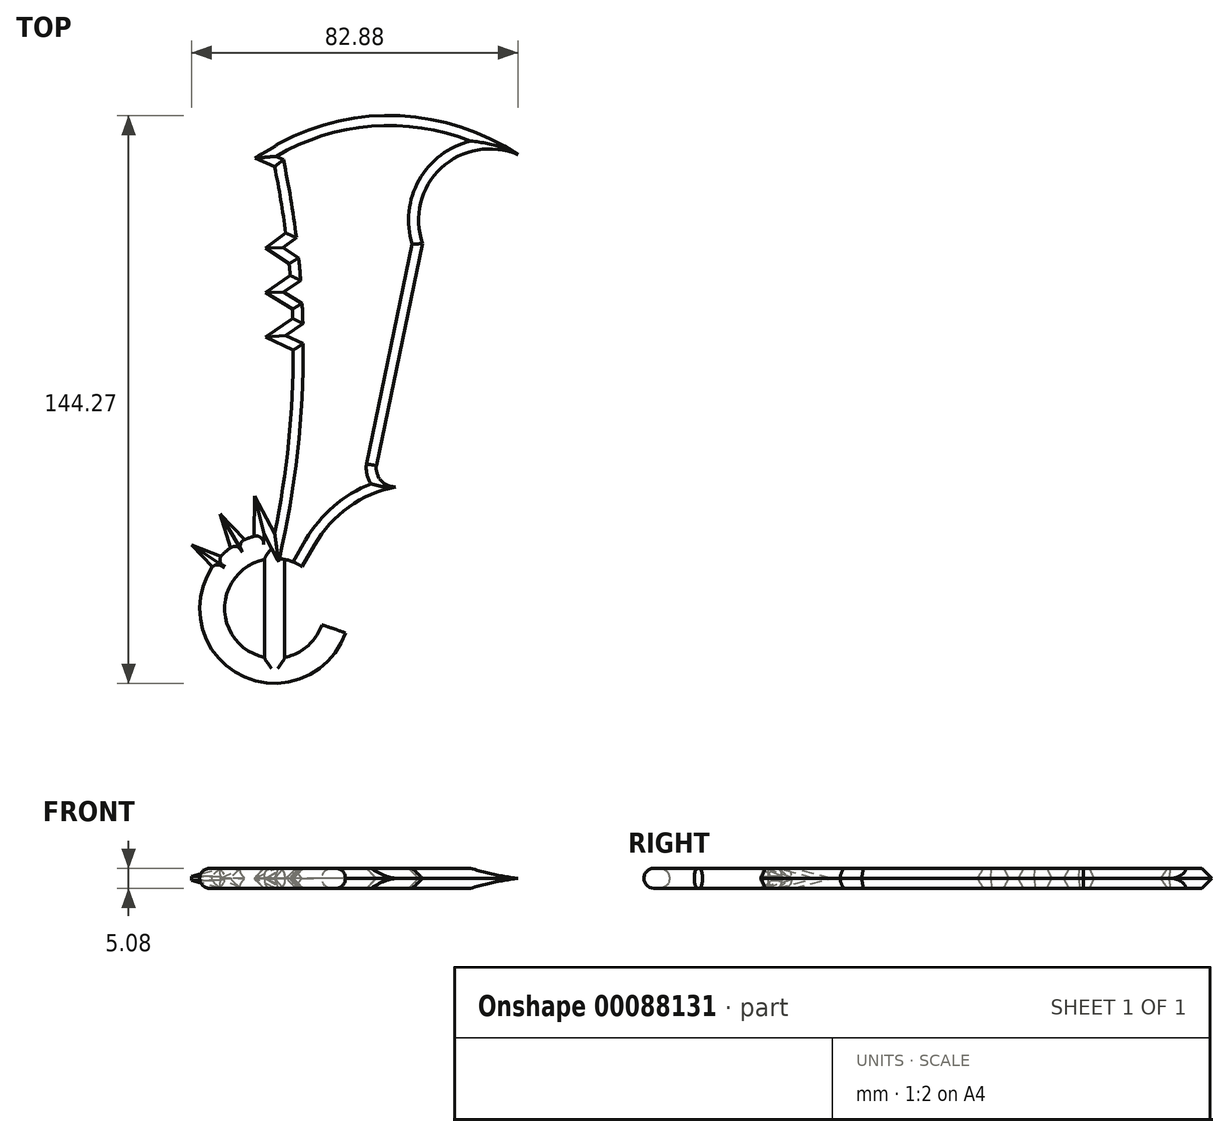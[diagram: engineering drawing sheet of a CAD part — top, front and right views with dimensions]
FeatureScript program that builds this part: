
annotation { "Feature Type Name" : "Feature", "Feature Type Description" : "" }
export const myFeature = defineFeature(function(context is Context, id is Id, definition is map)
    precondition{}
    {
        {
            var Q0;
            Q0=qCreatedBy(makeId("Top.planeOp"),FACE);
            var sketch = newSketch(context, id + "F0", { "sketchPlane" : qUnion([Q0])});
            skArc(sketch, "E0", {"start": v(10.12, 16.14) * mm, "mid": v(5.26, 18.3) * mm, "end": v(0, 19.05) * mm});
            skArc(sketch, "E1", {"start": v(6.94, 10.64) * mm, "mid": v(-12.02, -4.11) * mm, "end": v(12, -4.15) * mm});
            skLineSegment(sketch, "E2", {"start": v(0, 0) * mm, "end": v(-2.54, 0) * mm});
            skLineSegment(sketch, "E3", {"start": v(0, 0) * mm, "end": v(2.54, 0) * mm});
            skLineSegment(sketch, "E4", {"start": v(2.54, 0) * mm, "end": v(2.54, 12.44) * mm});
            skLineSegment(sketch, "E5", {"start": v(-2.54, 12.44) * mm, "end": v(-2.54, -12.44) * mm});
            skLineSegment(sketch, "E6", {"start": v(2.54, 0) * mm, "end": v(2.54, -12.44) * mm});
            skLineSegment(sketch, "E7", {"start": v(6.94, 10.64) * mm, "end": v(10.12, 16.14) * mm});
            skLineSegment(sketch, "E8", {"start": v(12, -4.15) * mm, "end": v(18, -6.23) * mm});
            skArc(sketch, "E9", {"start": v(0, 19.05) * mm, "mid": v(3.55, 42.22) * mm, "end": v(4.74, 65.62) * mm});
            skArc(sketch, "E10", {"start": v(61.8, 115.25) * mm, "mid": v(31.92, 125.15) * mm, "end": v(1.21, 118.24) * mm});
            skLineSegment(sketch, "E11", {"start": v(2.82, 95.35) * mm, "end": v(-2.36, 91.51) * mm});
            skLineSegment(sketch, "E12", {"start": v(3.7, 87.56) * mm, "end": v(-2.36, 91.51) * mm});
            skLineSegment(sketch, "E13", {"start": v(3.96, 84.58) * mm, "end": v(-2.36, 80.2) * mm});
            skLineSegment(sketch, "E14", {"start": v(4.5, 76.03) * mm, "end": v(-2.36, 80.2) * mm});
            skLineSegment(sketch, "E15", {"start": v(4.6, 73.66) * mm, "end": v(-2.36, 68.93) * mm});
            skLineSegment(sketch, "E16", {"start": v(4.74, 65.62) * mm, "end": v(-2.36, 68.93) * mm});
            skArc(sketch, "E17", {"start": v(-5.42, 114.55) * mm, "mid": v(-1.97, 116.17) * mm, "end": v(1.21, 118.24) * mm});
            skLineSegment(sketch, "E18", {"start": v(0, 112.2) * mm, "end": v(-5.42, 114.55) * mm});
            skArc(sketch, "E19", {"start": v(61.8, 115.25) * mm, "mid": v(42.32, 111.9) * mm, "end": v(37.6, 92.69) * mm});
            skArc(sketch, "E20", {"start": v(30.78, 30.87) * mm, "mid": v(18.85, 25.75) * mm, "end": v(10.12, 16.14) * mm});
            skArc(sketch, "E21", {"start": v(25.84, 36.28) * mm, "mid": v(27.07, 32.44) * mm, "end": v(30.78, 30.87) * mm});
            skArc(sketch, "E22.trimOffspring", {"start": v(4.6, 73.66) * mm, "mid": v(4.55, 74.85) * mm, "end": v(4.5, 76.03) * mm});
            skArc(sketch, "E23.trimOffspring", {"start": v(3.96, 84.58) * mm, "mid": v(3.83, 86.07) * mm, "end": v(3.7, 87.56) * mm});
            skArc(sketch, "E24.trimOffspring", {"start": v(2.82, 95.35) * mm, "mid": v(1.57, 103.8) * mm, "end": v(0, 112.2) * mm});
            skLineSegment(sketch, "E25", {"start": v(-2.54, 0) * mm, "end": v(0, 0) * mm});
            skLineSegment(sketch, "E26", {"start": v(0, 19.05) * mm, "end": v(-5.05, 28.6) * mm});
            skLineSegment(sketch, "E27", {"start": v(-5.05, 28.6) * mm, "end": v(-5.2, 18.33) * mm});
            skLineSegment(sketch, "E28", {"start": v(-7.62, 17.46) * mm, "end": v(-13.82, 24.04) * mm});
            skLineSegment(sketch, "E29", {"start": v(-13.82, 24.04) * mm, "end": v(-11.22, 15.4) * mm});
            skLineSegment(sketch, "E30", {"start": v(-13.67, 13.27) * mm, "end": v(-21.07, 16.12) * mm});
            skLineSegment(sketch, "E31", {"start": v(-21.07, 16.12) * mm, "end": v(-15.86, 10.55) * mm});
            skArc(sketch, "E32.trimOffspring", {"start": v(-5.2, 18.33) * mm, "mid": v(-6.43, 17.93) * mm, "end": v(-7.62, 17.46) * mm});
            skArc(sketch, "E33.trimOffspring", {"start": v(-11.22, 15.4) * mm, "mid": v(-12.49, 14.39) * mm, "end": v(-13.67, 13.27) * mm});
            skArc(sketch, "E34.trimOffspring", {"start": v(-15.86, 10.55) * mm, "mid": v(-8.46, -17.07) * mm, "end": v(18, -6.23) * mm});
            skLineSegment(sketch, "E35", {"start": v(25.84, 36.28) * mm, "end": v(37.6, 92.69) * mm});
            skSolve(sketch);
        }
        {
            var Q0;
            Q0 = qSketchRegion(id + "F0", true);
            extrude(context, id + "F1", {"entities" : qUnion([Q0]), "depth" : 5.08 * mm});
        }
        {
            var Q0;
            Q0=makeQuery(id+"F1.opExtrude","CAP_EDGE",EDGE,{"disambiguationData":[OSD([sQuery(id+"F0.wireOp",EDGE,"E35")])],"isStart":false});
            var Q1;
            Q1=makeQuery(id+"F1.opExtrude","CAP_EDGE",EDGE,{"disambiguationData":[OSD([sQuery(id+"F0.wireOp",EDGE,"E35")])],"isStart":true});
            chamfer(context, id + "F2", {"entities" : qUnion([Q0, Q1]), "width" : 2.54 * mm, "tangentPropagation" : true});
        }
        {
            var Q0;
            Q0=makeQuery(id+"F1.opExtrude","CAP_EDGE",EDGE,{"disambiguationData":[OSD([sQuery(id+"F0.wireOp",EDGE,"E19")])],"isStart":false});
            var Q1;
            Q1=makeQuery(id+"F1.opExtrude","CAP_EDGE",EDGE,{"disambiguationData":[OSD([sQuery(id+"F0.wireOp",EDGE,"E19")])],"isStart":true});
            chamfer(context, id + "F3", {"entities" : qUnion([Q0, Q1]), "width" : 2.54 * mm, "tangentPropagation" : true});
        }
        {
            var Q0;
            Q0=makeQuery(id+"F1.opExtrude","CAP_EDGE",EDGE,{"disambiguationData":[OSD([sQuery(id+"F0.wireOp",EDGE,"E10")])],"isStart":true});
            var Q1;
            Q1=makeQuery(id+"F1.opExtrude","CAP_EDGE",EDGE,{"disambiguationData":[OSD([sQuery(id+"F0.wireOp",EDGE,"E10")])],"isStart":false});
            chamfer(context, id + "F4", {"entities" : qUnion([Q0, Q1]), "width" : 2.54 * mm, "tangentPropagation" : true});
        }
        {
            var Q0;
            Q0=makeQuery(id+"F1.opExtrude","CAP_EDGE",EDGE,{"disambiguationData":[OSD([sQuery(id+"F0.wireOp",EDGE,"E24.trimOffspring")])],"isStart":true});
            var Q1;
            Q1=makeQuery(id+"F1.opExtrude","CAP_EDGE",EDGE,{"disambiguationData":[OSD([sQuery(id+"F0.wireOp",EDGE,"E24.trimOffspring")])],"isStart":false});
            chamfer(context, id + "F5", {"entities" : qUnion([Q0, Q1]), "width" : 2.54 * mm, "tangentPropagation" : true});
        }
        {
            var Q0;
            Q0=makeQuery(id+"F1.opExtrude","CAP_EDGE",EDGE,{"disambiguationData":[OSD([sQuery(id+"F0.wireOp",EDGE,"E18")])],"isStart":false});
            var Q1;
            Q1=makeQuery(id+"F1.opExtrude","CAP_EDGE",EDGE,{"disambiguationData":[OSD([sQuery(id+"F0.wireOp",EDGE,"E18")])],"isStart":true});
            chamfer(context, id + "F6", {"entities" : qUnion([Q0, Q1]), "width" : 2.54 * mm, "tangentPropagation" : true});
        }
        {
            var Q0;
            Q0=makeQuery(id+"F1.opExtrude","CAP_EDGE",EDGE,{"disambiguationData":[OSD([sQuery(id+"F0.wireOp",EDGE,"E9")])],"isStart":true});
            var Q1;
            Q1=makeQuery(id+"F1.opExtrude","CAP_EDGE",EDGE,{"disambiguationData":[OSD([sQuery(id+"F0.wireOp",EDGE,"E9")])],"isStart":false});
            chamfer(context, id + "F7", {"entities" : qUnion([Q0, Q1]), "width" : 2.54 * mm, "tangentPropagation" : true});
        }
        {
            var Q0;
            Q0=makeQuery(id+"F1.opExtrude","CAP_EDGE",EDGE,{"disambiguationData":[OSD([sQuery(id+"F0.wireOp",EDGE,"E16")])],"isStart":true});
            var Q1;
            Q1=makeQuery(id+"F1.opExtrude","CAP_EDGE",EDGE,{"disambiguationData":[OSD([sQuery(id+"F0.wireOp",EDGE,"E16")])],"isStart":false});
            var Q2;
            Q2=makeQuery(id+"F1.opExtrude","CAP_EDGE",EDGE,{"disambiguationData":[OSD([sQuery(id+"F0.wireOp",EDGE,"E15")])],"isStart":true});
            var Q3;
            Q3=makeQuery(id+"F1.opExtrude","CAP_EDGE",EDGE,{"disambiguationData":[OSD([sQuery(id+"F0.wireOp",EDGE,"E15")])],"isStart":false});
            var Q4;
            Q4=makeQuery(id+"F1.opExtrude","CAP_EDGE",EDGE,{"disambiguationData":[OSD([sQuery(id+"F0.wireOp",EDGE,"E22.trimOffspring")])],"isStart":false});
            var Q5;
            Q5=makeQuery(id+"F1.opExtrude","CAP_EDGE",EDGE,{"disambiguationData":[OSD([sQuery(id+"F0.wireOp",EDGE,"E22.trimOffspring")])],"isStart":true});
            var Q6;
            Q6=makeQuery(id+"F1.opExtrude","CAP_EDGE",EDGE,{"disambiguationData":[OSD([sQuery(id+"F0.wireOp",EDGE,"E14")])],"isStart":true});
            var Q7;
            Q7=makeQuery(id+"F1.opExtrude","CAP_EDGE",EDGE,{"disambiguationData":[OSD([sQuery(id+"F0.wireOp",EDGE,"E14")])],"isStart":false});
            var Q8;
            Q8=makeQuery(id+"F1.opExtrude","CAP_EDGE",EDGE,{"disambiguationData":[OSD([sQuery(id+"F0.wireOp",EDGE,"E13")])],"isStart":false});
            var Q9;
            Q9=makeQuery(id+"F1.opExtrude","CAP_EDGE",EDGE,{"disambiguationData":[OSD([sQuery(id+"F0.wireOp",EDGE,"E13")])],"isStart":true});
            var Q10;
            Q10=makeQuery(id+"F1.opExtrude","CAP_EDGE",EDGE,{"disambiguationData":[OSD([sQuery(id+"F0.wireOp",EDGE,"E23.trimOffspring")])],"isStart":true});
            var Q11;
            Q11=makeQuery(id+"F1.opExtrude","CAP_EDGE",EDGE,{"disambiguationData":[OSD([sQuery(id+"F0.wireOp",EDGE,"E23.trimOffspring")])],"isStart":false});
            var Q12;
            Q12=makeQuery(id+"F1.opExtrude","CAP_EDGE",EDGE,{"disambiguationData":[OSD([sQuery(id+"F0.wireOp",EDGE,"E12")])],"isStart":false});
            var Q13;
            Q13=makeQuery(id+"F1.opExtrude","CAP_EDGE",EDGE,{"disambiguationData":[OSD([sQuery(id+"F0.wireOp",EDGE,"E12")])],"isStart":true});
            var Q14;
            Q14=makeQuery(id+"F1.opExtrude","CAP_EDGE",EDGE,{"disambiguationData":[OSD([sQuery(id+"F0.wireOp",EDGE,"E11")])],"isStart":true});
            var Q15;
            Q15=makeQuery(id+"F1.opExtrude","CAP_EDGE",EDGE,{"disambiguationData":[OSD([sQuery(id+"F0.wireOp",EDGE,"E11")])],"isStart":false});
            chamfer(context, id + "F8", {"entities" : qUnion([Q0, Q1, Q2, Q3, Q4, Q5, Q6, Q7, Q8, Q9, Q10, Q11, Q12, Q13, Q14, Q15]), "width" : 2.54 * mm, "tangentPropagation" : true});
        }
        {
            var Q0;
            Q0=makeQuery(id+"F1.opExtrude","CAP_EDGE",EDGE,{"disambiguationData":[OSD([sQuery(id+"F0.wireOp",EDGE,"E20")])],"isStart":false});
            var Q1;
            Q1=makeQuery(id+"F1.opExtrude","CAP_EDGE",EDGE,{"disambiguationData":[OSD([sQuery(id+"F0.wireOp",EDGE,"E20")])],"isStart":true});
            chamfer(context, id + "F9", {"entities" : qUnion([Q0, Q1]), "width" : 2.54 * mm, "tangentPropagation" : true});
        }
        {
            var Q0;
            Q0=makeQuery(id+"F1.opExtrude","CAP_EDGE",EDGE,{"disambiguationData":[OSD([sQuery(id+"F0.wireOp",EDGE,"E34.trimOffspring")])],"isStart":false});
            var Q1;
            Q1=makeQuery(id+"F1.opExtrude","CAP_EDGE",EDGE,{"disambiguationData":[OSD([sQuery(id+"F0.wireOp",EDGE,"E34.trimOffspring")])],"isStart":true});
            var Q2;
            {var subQ0=sQuery(id+"F0.wireOp",EDGE,"E1");Q2=makeQuery(id+"F1.opExtrude","CAP_EDGE",EDGE,{"disambiguationData":[OSD([subQ0]),TDD([makeQuery(id+"F0.imprint","IMPRINT",EDGE,{"disambiguationData":[TD([[makeQuery(id+"F0.imprint","INTERSECT",VERTEX,{"derivedFrom":[subQ0,sQuery(id+"F0.wireOp",EDGE,"E8")]}),1.0]])],"derivedFrom":subQ0})])],"isStart":false});}
            var Q3;
            {var subQ0=sQuery(id+"F0.wireOp",EDGE,"E5");var subQ1=sQuery(id+"F0.wireOp",EDGE,"E1");Q3=makeQuery(id+"F1.opExtrude","CAP_EDGE",EDGE,{"disambiguationData":[OSD([subQ1]),TDD([makeQuery(id+"F0.imprint","IMPRINT",EDGE,{"disambiguationData":[TD([[makeQuery(id+"F0.imprint","INTERSECT",VERTEX,{"disambiguationData":[OD(0.0)],"derivedFrom":[subQ1,subQ0]}),-1.0]])],"derivedFrom":subQ1})])],"isStart":false});}
            var Q4;
            {var subQ0=sQuery(id+"F0.wireOp",EDGE,"E5");var subQ1=sQuery(id+"F0.wireOp",EDGE,"E1");Q4=makeQuery(id+"F1.opExtrude","CAP_EDGE",EDGE,{"disambiguationData":[OSD([subQ1]),TDD([makeQuery(id+"F0.imprint","IMPRINT",EDGE,{"disambiguationData":[TD([[makeQuery(id+"F0.imprint","INTERSECT",VERTEX,{"disambiguationData":[OD(0.0)],"derivedFrom":[subQ1,subQ0]}),-1.0]])],"derivedFrom":subQ1})])],"isStart":true});}
            var Q5;
            {var subQ0=sQuery(id+"F0.wireOp",EDGE,"E1");Q5=makeQuery(id+"F1.opExtrude","CAP_EDGE",EDGE,{"disambiguationData":[OSD([subQ0]),TDD([makeQuery(id+"F0.imprint","IMPRINT",EDGE,{"disambiguationData":[TD([[makeQuery(id+"F0.imprint","INTERSECT",VERTEX,{"derivedFrom":[subQ0,sQuery(id+"F0.wireOp",EDGE,"E8")]}),1.0]])],"derivedFrom":subQ0})])],"isStart":true});}
            fillet(context, id + "F10", {"entities" : qUnion([Q0, Q1, Q2, Q3, Q4, Q5]), "radius" : 2.54 * mm, "tangentPropagation" : true, "allowEdgeOverflow" : false});
        }
        {
            var Q0;
            Q0=makeQuery(id+"F1.opExtrude","CAP_EDGE",EDGE,{"disambiguationData":[OSD([sQuery(id+"F0.wireOp",EDGE,"E32.trimOffspring")])],"isStart":true});
            var Q1;
            Q1=makeQuery(id+"F1.opExtrude","CAP_EDGE",EDGE,{"disambiguationData":[OSD([sQuery(id+"F0.wireOp",EDGE,"E33.trimOffspring")])],"isStart":true});
            var Q2;
            Q2=makeQuery(id+"F1.opExtrude","CAP_EDGE",EDGE,{"disambiguationData":[OSD([sQuery(id+"F0.wireOp",EDGE,"E32.trimOffspring")])],"isStart":false});
            var Q3;
            Q3=makeQuery(id+"F1.opExtrude","CAP_EDGE",EDGE,{"disambiguationData":[OSD([sQuery(id+"F0.wireOp",EDGE,"E33.trimOffspring")])],"isStart":false});
            fillet(context, id + "F11", {"entities" : qUnion([Q0, Q1, Q2, Q3]), "radius" : 2.54 * mm, "tangentPropagation" : true, "allowEdgeOverflow" : false});
        }
        {
            var Q0;
            Q0=makeQuery(id+"F1.opExtrude","CAP_EDGE",EDGE,{"disambiguationData":[OSD([sQuery(id+"F0.wireOp",EDGE,"E29")])],"isStart":false});
            var Q1;
            Q1=makeQuery(id+"F1.opExtrude","CAP_EDGE",EDGE,{"disambiguationData":[OSD([sQuery(id+"F0.wireOp",EDGE,"E28")])],"isStart":false});
            var Q2;
            Q2=makeQuery(id+"F1.opExtrude","CAP_EDGE",EDGE,{"disambiguationData":[OSD([sQuery(id+"F0.wireOp",EDGE,"E27")])],"isStart":false});
            var Q3;
            Q3=makeQuery(id+"F1.opExtrude","CAP_EDGE",EDGE,{"disambiguationData":[OSD([sQuery(id+"F0.wireOp",EDGE,"E26")])],"isStart":false});
            var Q4;
            Q4=makeQuery(id+"F1.opExtrude","CAP_EDGE",EDGE,{"disambiguationData":[OSD([sQuery(id+"F0.wireOp",EDGE,"E27")])],"isStart":true});
            var Q5;
            Q5=makeQuery(id+"F1.opExtrude","CAP_EDGE",EDGE,{"disambiguationData":[OSD([sQuery(id+"F0.wireOp",EDGE,"E29")])],"isStart":true});
            var Q6;
            Q6=makeQuery(id+"F1.opExtrude","CAP_EDGE",EDGE,{"disambiguationData":[OSD([sQuery(id+"F0.wireOp",EDGE,"E28")])],"isStart":true});
            var Q7;
            Q7=makeQuery(id+"F1.opExtrude","CAP_EDGE",EDGE,{"disambiguationData":[OSD([sQuery(id+"F0.wireOp",EDGE,"E26")])],"isStart":true});
            chamfer(context, id + "F12", {"entities" : qUnion([Q0, Q1, Q2, Q3, Q4, Q5, Q6, Q7]), "width" : 2.5 * mm, "tangentPropagation" : true});
        }
        {
            var Q0;
            Q0=makeQuery(id+"F1.opExtrude","CAP_EDGE",EDGE,{"disambiguationData":[OSD([sQuery(id+"F0.wireOp",EDGE,"E31")])],"isStart":false});
            var Q1;
            Q1=makeQuery(id+"F1.opExtrude","CAP_EDGE",EDGE,{"disambiguationData":[OSD([sQuery(id+"F0.wireOp",EDGE,"E30")])],"isStart":false});
            var Q2;
            Q2=makeQuery(id+"F1.opExtrude","CAP_EDGE",EDGE,{"disambiguationData":[OSD([sQuery(id+"F0.wireOp",EDGE,"E31")])],"isStart":true});
            var Q3;
            Q3=makeQuery(id+"F1.opExtrude","CAP_EDGE",EDGE,{"disambiguationData":[OSD([sQuery(id+"F0.wireOp",EDGE,"E30")])],"isStart":true});
            chamfer(context, id + "F13", {"entities" : qUnion([Q0, Q1, Q2, Q3]), "width" : 2.03 * mm});
        }
        {
            var Q0;
            Q0=makeQuery(id+"F1.opExtrude","CAP_EDGE",EDGE,{"disambiguationData":[OSD([sQuery(id+"F0.wireOp",EDGE,"E4"),sQuery(id+"F0.wireOp",EDGE,"E6")])],"isStart":false});
            var Q1;
            Q1=makeQuery(id+"F1.opExtrude","CAP_EDGE",EDGE,{"disambiguationData":[OSD([sQuery(id+"F0.wireOp",EDGE,"E5")])],"isStart":false});
            var Q2;
            Q2=makeQuery(id+"F1.opExtrude","CAP_EDGE",EDGE,{"disambiguationData":[OSD([sQuery(id+"F0.wireOp",EDGE,"E5")])],"isStart":true});
            var Q3;
            Q3=makeQuery(id+"F1.opExtrude","CAP_EDGE",EDGE,{"disambiguationData":[OSD([sQuery(id+"F0.wireOp",EDGE,"E4"),sQuery(id+"F0.wireOp",EDGE,"E6")])],"isStart":true});
            fillet(context, id + "F14", {"entities" : qUnion([Q0, Q1, Q2, Q3]), "radius" : 1.78 * mm, "tangentPropagation" : true, "allowEdgeOverflow" : false});
        }
    });
